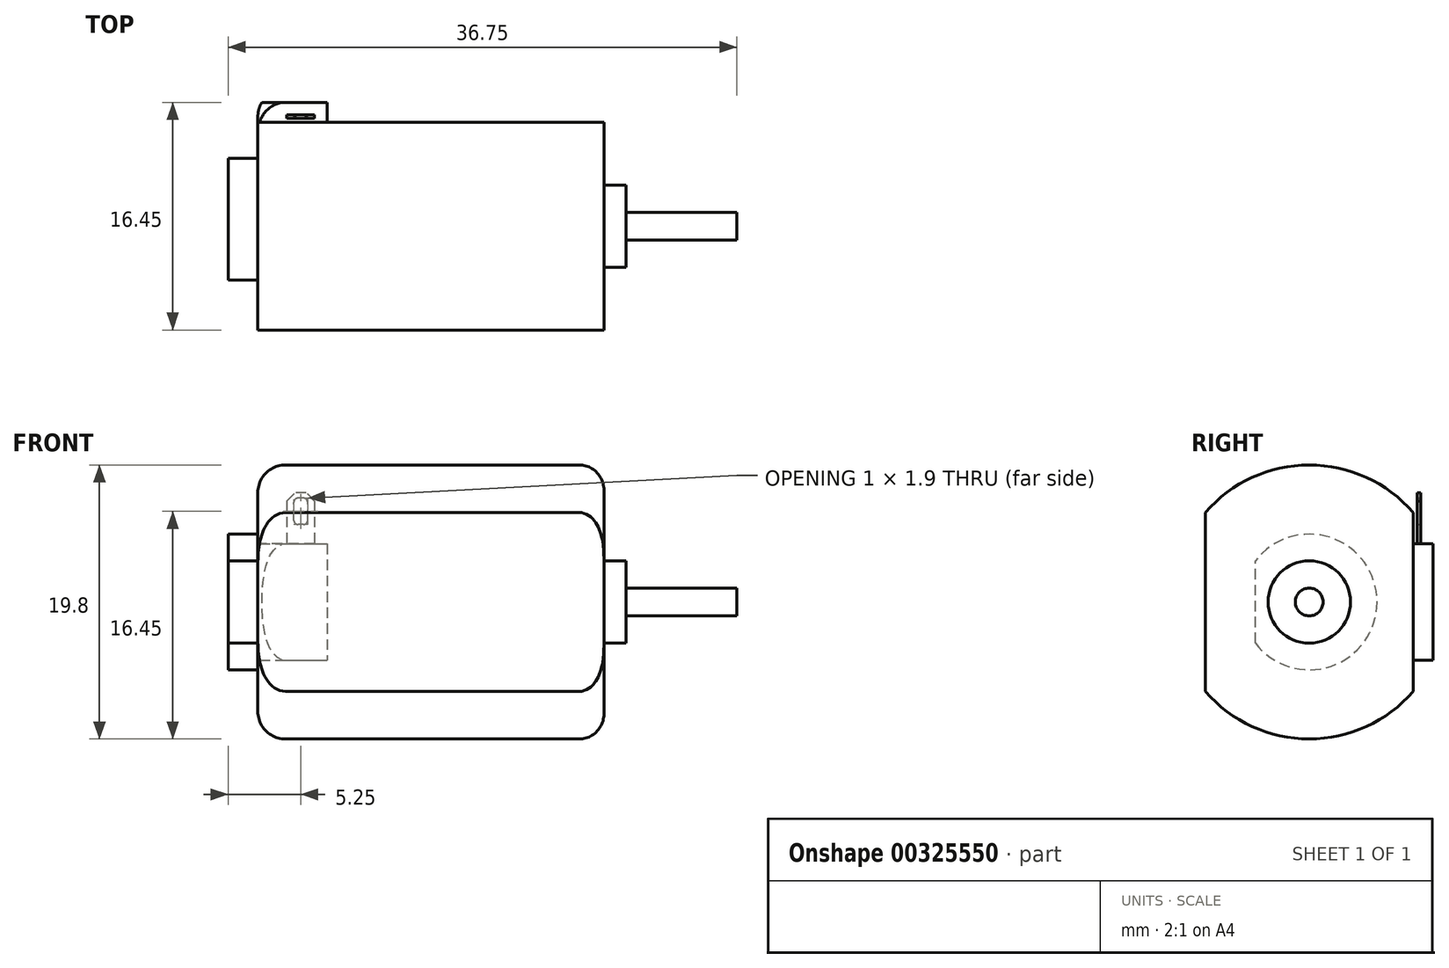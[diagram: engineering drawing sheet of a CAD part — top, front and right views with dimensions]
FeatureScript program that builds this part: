
annotation { "Feature Type Name" : "Feature", "Feature Type Description" : "" }
export const myFeature = defineFeature(function(context is Context, id is Id, definition is map)
    precondition{}
    {
        {
            var Q0;
            Q0=qCreatedBy(makeId("Front.planeOp"),FACE);
            var sketch = newSketch(context, id + "F0", { "sketchPlane" : qUnion([Q0])});
            skLineSegment(sketch, "E0.bottom", {"start": v(-25.3, 11.2) * mm, "end": v(7.6, 11.2) * mm});
            skLineSegment(sketch, "E0.top", {"start": v(-25.3, -11.2) * mm, "end": v(7.6, -11.2) * mm});
            skLineSegment(sketch, "E0.left", {"start": v(-25.3, 11.2) * mm, "end": v(-25.3, -11.2) * mm});
            skLineSegment(sketch, "E0.right", {"start": v(11.6, 7.2) * mm, "end": v(11.6, -7.2) * mm});
            skLineSegment(sketch, "E1", {"start": v(0, 0) * mm, "end": v(11.6, 0) * mm, "construction": true});
            skCircle(sketch, "E2", {"center": v(0, 0) * mm, "radius": 2.67 * mm});
            skPoint(sketch, "E3.visualSharp", {"position": v(11.6, 11.2) * mm});
            skArc(sketch, "E3.filletArc", {"start": v(11.6, 7.2) * mm, "mid": v(10.43, 10.03) * mm, "end": v(7.6, 11.2) * mm});
            skPoint(sketch, "E4.visualSharp", {"position": v(11.6, -11.2) * mm});
            skArc(sketch, "E4.filletArc", {"start": v(7.6, -11.2) * mm, "mid": v(10.43, -10.03) * mm, "end": v(11.6, -7.2) * mm});
            skCircle(sketch, "E5", {"center": v(-20.4, 8.75) * mm, "radius": 1.5 * mm});
            skCircle(sketch, "E6", {"center": v(-20.4, -8.75) * mm, "radius": 1.5 * mm});
            skLineSegment(sketch, "E7", {"start": v(-20.4, 8.75) * mm, "end": v(-20.4, 0) * mm, "construction": true});
            skLineSegment(sketch, "E8", {"start": v(-20.4, 0) * mm, "end": v(-20.4, -8.75) * mm, "construction": true});
            skSolve(sketch);
        }
        {
            var Q0;
            Q0=qSketchRegion(id+"F0",true);
            extrude(context, id + "F1", {"entities" : qUnion([Q0]), "depth" : 10 * mm});
        }
        {
            var Q0;
            Q0=qSketchRegion(id+"F0",true);
            extrude(context, id + "F2", {"entities" : qUnion([Q0]), "operationType" : NewBodyOperationType.ADD, "oppositeDirection" : true, "depth" : 8.6 * mm});
        }
        {
            var Q0;
            {var subQ0=sQuery(id+"F0.wireOp",EDGE,"E0.left");Q0=makeQuery(id+"F2.boolean.opBoolean","MERGE",FACE,{"derivedFrom":[makeQuery(id+"F1.opExtrude","SWEPT_FACE",FACE,{"disambiguationData":[OSD([subQ0])]}),makeQuery(id+"F2.opExtrude","SWEPT_FACE",FACE,{"disambiguationData":[OSD([subQ0])]})]});}
            var sketch = newSketch(context, id + "F3", { "sketchPlane" : qUnion([Q0])});
            skArc(sketch, "E9", {"start": v(-8.6, -7.17) * mm, "mid": v(0, -11.2) * mm, "end": v(8.6, -7.17) * mm});
            skLineSegment(sketch, "E10", {"start": v(8.6, -7.17) * mm, "end": v(8.6, 7.17) * mm});
            skLineSegment(sketch, "E11.0", {"start": v(-8.6, 7.17) * mm, "end": v(-8.6, -7.17) * mm});
            skPoint(sketch, "E12.orphan", {"position": v(-8.6, -11.2) * mm});
            skPoint(sketch, "E13.orphan", {"position": v(-8.6, 11.2) * mm});
            skArc(sketch, "E14.trimOffspring", {"start": v(8.6, 7.17) * mm, "mid": v(0, 11.2) * mm, "end": v(-8.6, 7.17) * mm});
            skSolve(sketch);
        }
        {
            var Q0;
            Q0=qSketchRegion(id+"F3",true);
            extrude(context, id + "F4", {"entities" : qUnion([Q0]), "operationType" : NewBodyOperationType.ADD, "depth" : 11.5 * mm});
        }
        {
            var Q0;
            Q0=makeQuery(id+"F4.opExtrude","CAP_FACE",FACE,{"disambiguationData":[OSD([sQuery(id+"F3.wireOp",EDGE,"E9"),sQuery(id+"F3.wireOp",EDGE,"E10"),sQuery(id+"F3.wireOp",EDGE,"E11.0"),sQuery(id+"F3.wireOp",EDGE,"E14.trimOffspring")])],"isStart":false});
            var sketch = newSketch(context, id + "F5", { "sketchPlane" : qUnion([Q0])});
            skArc(sketch, "E15", {"start": v(7.5, 6.46) * mm, "mid": v(0, 9.9) * mm, "end": v(-7.5, 6.46) * mm});
            skLineSegment(sketch, "E16", {"start": v(7.5, -6.46) * mm, "end": v(7.5, 6.46) * mm});
            skLineSegment(sketch, "E17", {"start": v(-7.5, -6.46) * mm, "end": v(-7.5, 6.46) * mm});
            skArc(sketch, "E18.trimOffspring", {"start": v(-7.5, -6.46) * mm, "mid": v(0, -9.9) * mm, "end": v(7.5, -6.46) * mm});
            skSolve(sketch);
        }
        {
            var Q0;
            Q0=qSketchRegion(id+"F5",true);
            extrude(context, id + "F6", {"entities" : qUnion([Q0]), "operationType" : NewBodyOperationType.ADD, "depth" : 13.45 * mm});
        }
        {
            var Q0;
            Q0=makeQuery(id+"F6.opExtrude","CAP_FACE",FACE,{"disambiguationData":[OSD([sQuery(id+"F5.wireOp",EDGE,"E15"),sQuery(id+"F5.wireOp",EDGE,"E16"),sQuery(id+"F5.wireOp",EDGE,"E17"),sQuery(id+"F5.wireOp",EDGE,"E18.trimOffspring")])],"isStart":false});
            var sketch = newSketch(context, id + "F7", { "sketchPlane" : qUnion([Q0])});
            skArc(sketch, "E19", {"start": v(3.9, 2.97) * mm, "mid": v(-4.9, 0) * mm, "end": v(3.9, -2.97) * mm});
            skLineSegment(sketch, "E20", {"start": v(3.9, -2.97) * mm, "end": v(3.9, 2.97) * mm});
            skSolve(sketch);
        }
        {
            var Q0;
            Q0=qSketchRegion(id+"F7",true);
            extrude(context, id + "F8", {"entities" : qUnion([Q0]), "operationType" : NewBodyOperationType.ADD, "depth" : 2.15 * mm});
        }
        {
            var Q0;
            Q0=makeQuery(id+"F6.opExtrude","SWEPT_FACE",FACE,{"disambiguationData":[OSD([sQuery(id+"F5.wireOp",EDGE,"E17")])]});
            var sketch = newSketch(context, id + "F9", { "sketchPlane" : qUnion([Q0])});
            skLineSegment(sketch, "E21.bottom", {"start": v(50.25, 4.2) * mm, "end": v(45.25, 4.2) * mm});
            skLineSegment(sketch, "E21.top", {"start": v(50.25, -4.2) * mm, "end": v(45.25, -4.2) * mm});
            skLineSegment(sketch, "E21.left", {"start": v(50.25, 4.2) * mm, "end": v(50.25, -4.2) * mm});
            skLineSegment(sketch, "E21.right", {"start": v(45.25, 4.2) * mm, "end": v(45.25, -4.2) * mm});
            skLineSegment(sketch, "E22", {"start": v(0, 0) * mm, "end": v(45.25, 0) * mm, "construction": true});
            skSolve(sketch);
        }
        {
            var Q0;
            Q0=qSketchRegion(id+"F9",true);
            extrude(context, id + "F10", {"entities" : qUnion([Q0]), "operationType" : NewBodyOperationType.ADD, "depth" : 1.45 * mm});
        }
        {
            var Q0;
            Q0=makeQuery(id+"F6.opExtrude","CAP_EDGE",EDGE,{"disambiguationData":[OSD([sQuery(id+"F5.wireOp",EDGE,"E15")])],"isStart":false});
            fillet(context, id + "F11", {"entities" : qUnion([Q0]), "radius" : 2 * mm, "tangentPropagation" : true, "allowEdgeOverflow" : false});
        }
        {
            var Q0;
            Q0=makeQuery(id+"F10.opExtrude","SWEPT_FACE",FACE,{"disambiguationData":[OSD([sQuery(id+"F9.wireOp",EDGE,"E21.bottom")])]});
            var sketch = newSketch(context, id + "F12", { "sketchPlane" : qUnion([Q0])});
            skLineSegment(sketch, "E23.bottom", {"start": v(-46.15, 8.05) * mm, "end": v(-48.15, 8.05) * mm});
            skLineSegment(sketch, "E23.top", {"start": v(-46.15, 7.8) * mm, "end": v(-48.15, 7.8) * mm});
            skLineSegment(sketch, "E23.left", {"start": v(-46.15, 8.05) * mm, "end": v(-46.15, 7.8) * mm});
            skLineSegment(sketch, "E23.right", {"start": v(-48.15, 8.05) * mm, "end": v(-48.15, 7.8) * mm});
            skSolve(sketch);
        }
        {
            var Q0;
            Q0=qSketchRegion(id+"F12",true);
            extrude(context, id + "F13", {"entities" : qUnion([Q0]), "operationType" : NewBodyOperationType.ADD, "depth" : 3.7 * mm});
        }
        {
            var Q0;
            Q0=makeQuery(id+"F13.opExtrude","SWEPT_FACE",FACE,{"disambiguationData":[OSD([sQuery(id+"F12.wireOp",EDGE,"E23.bottom")])]});
            var sketch = newSketch(context, id + "F14", { "sketchPlane" : qUnion([Q0])});
            skLineSegment(sketch, "E24.bottom", {"start": v(46.95, 5.6) * mm, "end": v(47.35, 5.6) * mm});
            skLineSegment(sketch, "E24.top", {"start": v(46.95, 7.5) * mm, "end": v(47.35, 7.5) * mm});
            skLineSegment(sketch, "E24.left", {"start": v(46.65, 5.9) * mm, "end": v(46.65, 7.2) * mm});
            skLineSegment(sketch, "E24.right", {"start": v(47.65, 5.9) * mm, "end": v(47.65, 7.2) * mm});
            skLineSegment(sketch, "E25", {"start": v(47.15, 7.5) * mm, "end": v(47.15, 7.9) * mm, "construction": true});
            skPoint(sketch, "E26.visualSharp", {"position": v(46.65, 5.6) * mm});
            skArc(sketch, "E26.filletArc", {"start": v(46.65, 5.9) * mm, "mid": v(46.74, 5.69) * mm, "end": v(46.95, 5.6) * mm});
            skPoint(sketch, "E27.visualSharp", {"position": v(46.65, 7.5) * mm});
            skArc(sketch, "E27.filletArc", {"start": v(46.95, 7.5) * mm, "mid": v(46.74, 7.41) * mm, "end": v(46.65, 7.2) * mm});
            skPoint(sketch, "E28.visualSharp", {"position": v(47.65, 7.5) * mm});
            skArc(sketch, "E28.filletArc", {"start": v(47.65, 7.2) * mm, "mid": v(47.56, 7.41) * mm, "end": v(47.35, 7.5) * mm});
            skPoint(sketch, "E29.visualSharp", {"position": v(47.65, 5.6) * mm});
            skArc(sketch, "E29.filletArc", {"start": v(47.35, 5.6) * mm, "mid": v(47.56, 5.69) * mm, "end": v(47.65, 5.9) * mm});
            skSolve(sketch);
        }
        {
            var Q0;
            Q0=qSketchRegion(id+"F14",true);
            extrude(context, id + "F15", {"entities" : qUnion([Q0]), "operationType" : NewBodyOperationType.REMOVE, "endBound" : BoundingType.UP_TO_NEXT, "oppositeDirection" : true, "depth" : 25 * mm});
        }
        {
            var Q0;
            Q0=makeQuery(id+"F13.opExtrude","CAP_EDGE",EDGE,{"disambiguationData":[OSD([sQuery(id+"F12.wireOp",EDGE,"E23.left")])],"isStart":false});
            var Q1;
            Q1=makeQuery(id+"F13.opExtrude","CAP_EDGE",EDGE,{"disambiguationData":[OSD([sQuery(id+"F12.wireOp",EDGE,"E23.right")])],"isStart":false});
            chamfer(context, id + "F16", {"entities" : qUnion([Q0, Q1]), "width" : .6 * mm, "tangentPropagation" : true});
        }
        {
            var Q0;
            Q0=makeQuery(id+"F4.opExtrude","CAP_FACE",FACE,{"disambiguationData":[OSD([sQuery(id+"F3.wireOp",EDGE,"E9"),sQuery(id+"F3.wireOp",EDGE,"E10"),sQuery(id+"F3.wireOp",EDGE,"E11.0"),sQuery(id+"F3.wireOp",EDGE,"E14.trimOffspring")])],"isStart":false});
            var sketch = newSketch(context, id + "F17", { "sketchPlane" : qUnion([Q0])});
            skCircle(sketch, "E30", {"center": v(0, 0) * mm, "radius": 34 * mm});
            skSolve(sketch);
        }
        {
            var Q0;
            Q0 = qSketchRegion(id + "F17", true);
            extrude(context, id + "F18", {"entities" : qUnion([Q0]), "operationType" : NewBodyOperationType.REMOVE, "endBound" : BoundingType.THROUGH_ALL, "oppositeDirection" : true, "depth" : 25 * mm, "offsetDistance" : 25 * mm});
        }
        {
            var Q0;
            Q0=makeQuery(id+"F18.boolean.opBoolean","COPY",FACE,{"derivedFrom":makeQuery(id+"F18.opExtrude","CAP_FACE",FACE,{"disambiguationData":[OSD([sQuery(id+"F17.wireOp",EDGE,"E30")])],"isStart":true})});
            extrude(context, id + "F19", {"entities" : qUnion([Q0]), "operationType" : NewBodyOperationType.ADD, "depth" : (25 - 13.45) * mm, "offsetDistance" : 25 * mm});
        }
        {
            var Q0;
            Q0=makeQuery(id+"F19.opExtrude","CAP_FACE",FACE,{"disambiguationData":[OSD([sQuery(id+"F17.wireOp",EDGE,"E30")])],"isStart":false});
            var sketch = newSketch(context, id + "F20", { "sketchPlane" : qUnion([Q0])});
            skCircle(sketch, "E31", {"center": v(0, 0) * mm, "radius": 2.98 * mm});
            skSolve(sketch);
        }
        {
            var Q0;
            Q0 = qSketchRegion(id + "F20", true);
            extrude(context, id + "F21", {"entities" : qUnion([Q0]), "operationType" : NewBodyOperationType.ADD, "depth" : 1.6 * mm, "offsetDistance" : 25 * mm});
        }
        {
            var Q0;
            Q0=makeQuery(id+"F21.opExtrude","CAP_FACE",FACE,{"disambiguationData":[OSD([sQuery(id+"F20.wireOp",EDGE,"E31")])],"isStart":false});
            var sketch = newSketch(context, id + "F22", { "sketchPlane" : qUnion([Q0])});
            skCircle(sketch, "E32", {"center": v(0, 0) * mm, "radius": 1 * mm});
            skSolve(sketch);
        }
        {
            var Q0;
            Q0 = qSketchRegion(id + "F22", true);
            extrude(context, id + "F23", {"entities" : qUnion([Q0]), "operationType" : NewBodyOperationType.ADD, "depth" : 8 * mm, "offsetDistance" : 25 * mm});
        }
        {
            var Q0;
            Q0=makeQuery(id+"F19.opExtrude","CAP_EDGE",EDGE,{"disambiguationData":[OSD([sQuery(id+"F5.wireOp",EDGE,"E15")])],"isStart":false});
            var Q1;
            Q1=makeQuery(id+"F19.opExtrude","CAP_EDGE",EDGE,{"disambiguationData":[OSD([sQuery(id+"F5.wireOp",EDGE,"E18.trimOffspring")])],"isStart":false});
            fillet(context, id + "F24", {"entities" : qUnion([Q0, Q1]), "radius" : 1.8 * mm, "tangentPropagation" : true, "allowEdgeOverflow" : false});
        }
    });
